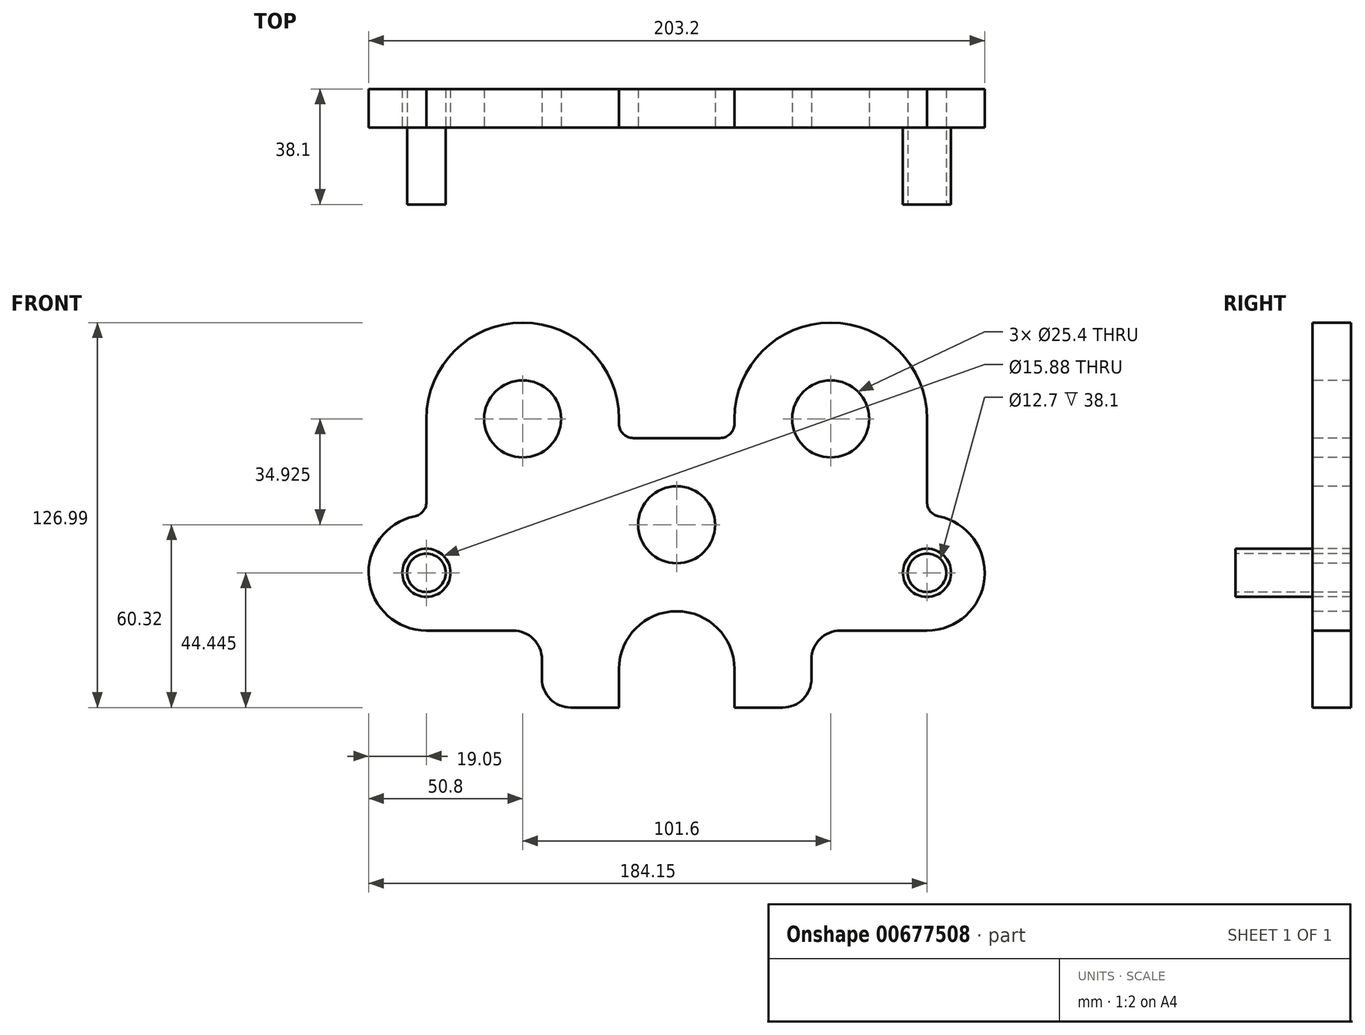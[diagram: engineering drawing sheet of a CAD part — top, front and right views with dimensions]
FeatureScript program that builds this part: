
annotation { "Feature Type Name" : "Feature", "Feature Type Description" : "" }
export const myFeature = defineFeature(function(context is Context, id is Id, definition is map)
    precondition{}
    {
        {
            var Q0;
            Q0=qCreatedBy(makeId("Front.planeOp"),FACE);
            var sketch = newSketch(context, id + "F0", { "sketchPlane" : qUnion([Q0])});
            skLineSegment(sketch, "E0", {"start": v(0, 76.7) * mm, "end": v(0, -75.9) * mm, "construction": true});
            skLineSegment(sketch, "E1", {"start": v(50.8, 76.08) * mm, "end": v(50.8, 12.52) * mm, "construction": true});
            skCircle(sketch, "E2", {"center": v(0, 0) * mm, "radius": 12.7 * mm});
            skCircle(sketch, "E3", {"center": v(50.8, 34.93) * mm, "radius": 12.7 * mm});
            skLineSegment(sketch, "E4", {"start": v(0, 28.58) * mm, "end": v(14.29, 28.58) * mm});
            skArc(sketch, "E5", {"start": v(82.55, 34.93) * mm, "mid": v(50.8, 66.68) * mm, "end": v(19.05, 34.93) * mm});
            skPoint(sketch, "E6.visualSharp", {"position": v(19.7, 28.58) * mm});
            skLineSegment(sketch, "E7", {"start": v(82.55, -34.92) * mm, "end": v(53.98, -34.92) * mm});
            skLineSegment(sketch, "E8", {"start": v(-29.42, 0) * mm, "end": v(25.25, 0) * mm, "construction": true});
            skCircle(sketch, "E9", {"center": v(82.55, -15.87) * mm, "radius": 6.35 * mm});
            skLineSegment(sketch, "E10", {"start": v(19.05, 34.93) * mm, "end": v(19.05, 33.34) * mm});
            skLineSegment(sketch, "E11", {"start": v(82.55, -7.94) * mm, "end": v(82.55, -31.6) * mm, "construction": true});
            skLineSegment(sketch, "E12", {"start": v(82.55, 34.93) * mm, "end": v(82.55, 7.46) * mm});
            skLineSegment(sketch, "E13", {"start": v(22.13, 34.93) * mm, "end": v(67.82, 34.93) * mm, "construction": true});
            skLineSegment(sketch, "E14", {"start": v(59.23, -15.87) * mm, "end": v(95.93, -15.87) * mm, "construction": true});
            skLineSegment(sketch, "E15", {"start": v(44.45, -44.45) * mm, "end": v(44.45, -50.8) * mm});
            skLineSegment(sketch, "E16", {"start": v(34.93, -60.32) * mm, "end": v(19.05, -60.32) * mm});
            skLineSegment(sketch, "E17", {"start": v(19.05, -60.32) * mm, "end": v(19.05, -47.62) * mm});
            skLineSegment(sketch, "E18.MirrorCS", {"start": v(0, 28.58) * mm, "end": v(-14.29, 28.58) * mm});
            skLineSegment(sketch, "E19.MirrorCS", {"start": v(-19.05, 34.93) * mm, "end": v(-19.05, 33.34) * mm});
            skArc(sketch, "E20.MirrorCS", {"start": v(-82.55, 34.93) * mm, "mid": v(-50.8, 66.68) * mm, "end": v(-19.05, 34.93) * mm});
            skLineSegment(sketch, "E21.MirrorCS", {"start": v(-82.55, 34.93) * mm, "end": v(-82.55, 7.46) * mm});
            skArc(sketch, "E22.MirrorCS", {"start": v(-82.55, -34.93) * mm, "mid": v(-101.5, -17.79) * mm, "end": v(-86.36, 2.8) * mm});
            skLineSegment(sketch, "E23.MirrorCS", {"start": v(-82.55, -34.93) * mm, "end": v(-53.97, -34.93) * mm});
            skLineSegment(sketch, "E24.MirrorCS", {"start": v(-44.45, -44.45) * mm, "end": v(-44.45, -50.8) * mm});
            skLineSegment(sketch, "E25.MirrorCS", {"start": v(-34.92, -60.32) * mm, "end": v(-19.05, -60.32) * mm});
            skLineSegment(sketch, "E26.MirrorCS", {"start": v(-19.05, -60.32) * mm, "end": v(-19.05, -47.62) * mm});
            skCircle(sketch, "E27.MirrorC", {"center": v(-50.8, 34.93) * mm, "radius": 12.7 * mm});
            skCircle(sketch, "E28.MirrorC", {"center": v(-82.55, -15.88) * mm, "radius": 6.35 * mm});
            skLineSegment(sketch, "E29.MirrorCS", {"start": v(-59.23, -15.87) * mm, "end": v(-95.93, -15.87) * mm, "construction": true});
            skLineSegment(sketch, "E30.MirrorCS", {"start": v(-82.55, -7.94) * mm, "end": v(-82.55, -31.6) * mm, "construction": true});
            skLineSegment(sketch, "E31.MirrorCS", {"start": v(-50.8, 76.08) * mm, "end": v(-50.8, 12.52) * mm, "construction": true});
            skLineSegment(sketch, "E32.MirrorCS", {"start": v(-22.13, 34.93) * mm, "end": v(-67.82, 34.93) * mm, "construction": true});
            skArc(sketch, "E33", {"start": v(19.05, -47.62) * mm, "mid": v(0, -28.57) * mm, "end": v(-19.05, -47.62) * mm});
            skPoint(sketch, "E34.visualSharp", {"position": v(-44.45, -34.92) * mm});
            skArc(sketch, "E34.filletArc", {"start": v(-44.45, -44.45) * mm, "mid": v(-47.24, -37.71) * mm, "end": v(-53.97, -34.93) * mm});
            skPoint(sketch, "E35.visualSharp", {"position": v(44.45, -34.92) * mm});
            skArc(sketch, "E35.filletArc", {"start": v(53.98, -34.92) * mm, "mid": v(47.24, -37.71) * mm, "end": v(44.45, -44.45) * mm});
            skPoint(sketch, "E36.visualSharp", {"position": v(44.45, -60.32) * mm});
            skArc(sketch, "E36.filletArc", {"start": v(34.93, -60.32) * mm, "mid": v(41.66, -57.54) * mm, "end": v(44.45, -50.8) * mm});
            skPoint(sketch, "E37.visualSharp", {"position": v(-44.45, -60.32) * mm});
            skArc(sketch, "E37.filletArc", {"start": v(-44.45, -50.8) * mm, "mid": v(-41.66, -57.54) * mm, "end": v(-34.92, -60.32) * mm});
            skLineSegment(sketch, "E38", {"start": v(0, -47.62) * mm, "end": v(26.3, -47.62) * mm, "construction": true});
            skLineSegment(sketch, "E39", {"start": v(26.3, -47.62) * mm, "end": v(-26.62, -47.62) * mm, "construction": true});
            skPoint(sketch, "E40.visualSharp", {"position": v(-82.55, 3.17) * mm});
            skArc(sketch, "E40.filletArc", {"start": v(-86.36, 2.8) * mm, "mid": v(-83.62, 4.44) * mm, "end": v(-82.55, 7.46) * mm});
            skArc(sketch, "E41.MirrorCS", {"start": v(82.55, -34.92) * mm, "mid": v(101.5, -17.79) * mm, "end": v(86.36, 2.8) * mm});
            skPoint(sketch, "E42.MirrorP", {"position": v(82.55, 3.18) * mm});
            skArc(sketch, "E43.MirrorCS", {"start": v(86.36, 2.8) * mm, "mid": v(83.62, 4.44) * mm, "end": v(82.55, 7.46) * mm});
            skPoint(sketch, "E44.visualSharp", {"position": v(-19.05, 28.57) * mm});
            skArc(sketch, "E44.filletArc", {"start": v(-19.05, 33.34) * mm, "mid": v(-17.66, 29.97) * mm, "end": v(-14.29, 28.58) * mm});
            skPoint(sketch, "E45.visualSharp", {"position": v(19.05, 28.58) * mm});
            skArc(sketch, "E45.filletArc", {"start": v(14.29, 28.58) * mm, "mid": v(17.66, 29.97) * mm, "end": v(19.05, 33.34) * mm});
            skCircle(sketch, "E46", {"center": v(82.55, -15.87) * mm, "radius": 7.94 * mm});
            skCircle(sketch, "E47", {"center": v(-82.55, -15.88) * mm, "radius": 7.94 * mm});
            skSolve(sketch);
        }
        {
            var Q0;
            Q0=qSketchRegion(id+"F0",true);
            var Q1;
            Q1=makeQuery(id+"F0.imprint","IMPRINT",FACE,{"disambiguationData":[TD([[makeQuery(id+"F0.imprint","IMPRINT",EDGE,{"derivedFrom":sQuery(id+"F0.wireOp",EDGE,"E9")}),-1.0]])]});
            var Q2;
            Q2=makeQuery(id+"F0.imprint","IMPRINT",FACE,{"disambiguationData":[TD([[makeQuery(id+"F0.imprint","IMPRINT",EDGE,{"derivedFrom":sQuery(id+"F0.wireOp",EDGE,"E28.MirrorC")}),1.0]])]});
            extrude(context, id + "F1", {"entities" : qUnion([Q0, Q1, Q2]), "oppositeDirection" : true, "depth" : 12.7 * mm, "offsetDistance" : 25.4 * mm});
        }
        {
            var Q0;
            Q0=makeQuery(id+"F0.imprint","IMPRINT",FACE,{"disambiguationData":[TD([[makeQuery(id+"F0.imprint","IMPRINT",EDGE,{"derivedFrom":sQuery(id+"F0.wireOp",EDGE,"E28.MirrorC")}),1.0]])]});
            var Q1;
            Q1=makeQuery(id+"F0.imprint","IMPRINT",FACE,{"disambiguationData":[TD([[makeQuery(id+"F0.imprint","IMPRINT",EDGE,{"derivedFrom":sQuery(id+"F0.wireOp",EDGE,"E9")}),-1.0]])]});
            extrude(context, id + "F2", {"entities" : qUnion([Q0, Q1]), "operationType" : NewBodyOperationType.ADD, "depth" : 25.4 * mm, "offsetDistance" : 25.4 * mm});
        }
    });
